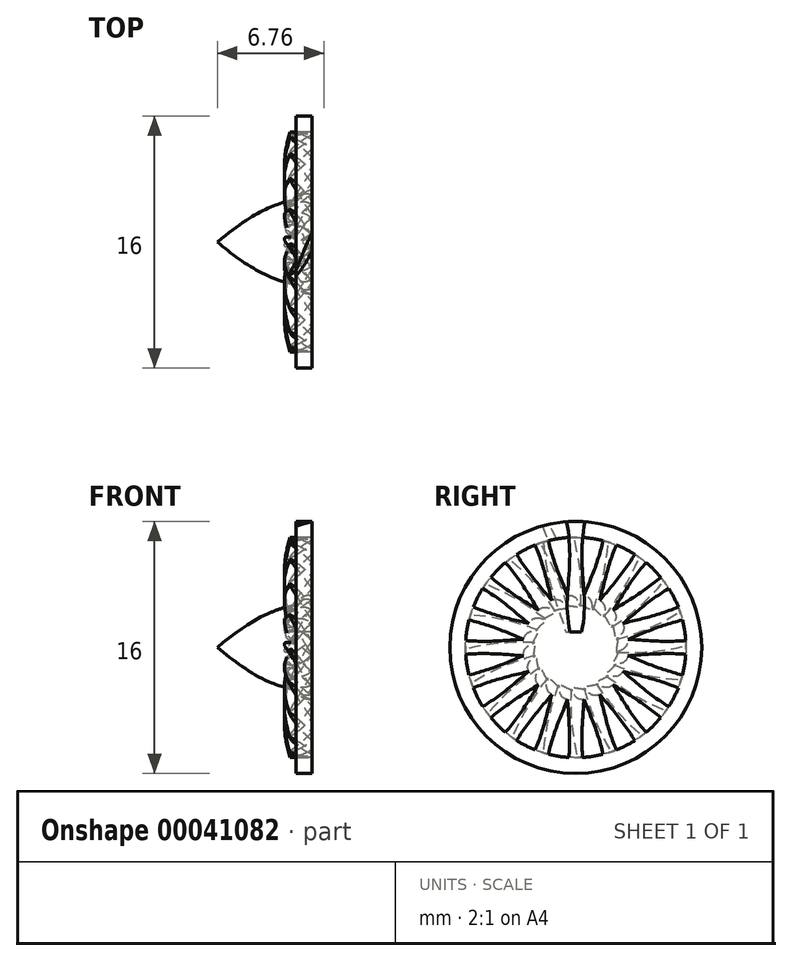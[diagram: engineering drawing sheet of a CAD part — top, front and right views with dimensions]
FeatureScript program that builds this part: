
annotation { "Feature Type Name" : "Feature", "Feature Type Description" : "" }
export const myFeature = defineFeature(function(context is Context, id is Id, definition is map)
    precondition{}
    {
        {
            var Q0;
            Q0=qCreatedBy(makeId("Top.planeOp"),FACE);
            var sketch = newSketch(context, id + "F0", { "sketchPlane" : qUnion([Q0])});
            skLineSegment(sketch, "E0", {"start": v(-70.31, 0) * mm, "end": v(56.67, 0) * mm, "construction": true});
            skLineSegment(sketch, "E1", {"start": v(0, 7) * mm, "end": v(-1, 7) * mm});
            skLineSegment(sketch, "E2", {"start": v(-1, 7) * mm, "end": v(-1, 8) * mm});
            skLineSegment(sketch, "E3", {"start": v(-1, 8) * mm, "end": v(-1, 8) * mm});
            skLineSegment(sketch, "E4", {"start": v(-1, 8) * mm, "end": v(0, 8) * mm});
            skLineSegment(sketch, "E5", {"start": v(0, 8) * mm, "end": v(0, 7) * mm});
            skLineSegment(sketch, "E6", {"start": v(0, 0) * mm, "end": v(0, 3) * mm});
            skLineSegment(sketch, "E7", {"start": v(-6, 0) * mm, "end": v(0, 0) * mm});
            skFitSpline(sketch, "E8", {"points": [v(0, 3) * mm, v(-6, 0) * mm], "startDerivative": vector(-5.94, -1.65) * mm, "endDerivative": vector(-8.8, -7.36) * mm});
            skSolve(sketch);
        }
        {
            var Q0;
            Q0=makeQuery(id+"F0.imprint","IMPRINT",FACE,{"disambiguationData":[TD([[makeQuery(id+"F0.imprint","IMPRINT",EDGE,{"derivedFrom":sQuery(id+"F0.wireOp",EDGE,"E1")}),-1.0]])]});
            var Q1;
            Q1=makeQuery(id+"F0.imprint","IMPRINT",FACE,{"disambiguationData":[TD([[makeQuery(id+"F0.imprint","IMPRINT",EDGE,{"derivedFrom":sQuery(id+"F0.wireOp",EDGE,"E6")}),1.0]])]});
            var Q2;
            Q2=sQuery(id+"F0.wireOp",EDGE,"E0");
            revolve(context, id + "F1", {"entities" : qUnion([Q0, Q1]), "axis" : qUnion([Q2]), "revolveType" : RevolveType.FULL});
        }
        {
            var Q0;
            Q0=qCreatedBy(makeId("Front.planeOp"),FACE);
            cPlane(context, id + "F2", {"entities" : qUnion([Q0]), "cplaneType" : CPlaneType.OFFSET, "offset" : 3.5 * mm, "width" : 150 * mm, "height" : 150 * mm});
        }
        {
            var Q0;
            Q0=qCreatedBy(makeId("Top.planeOp"),FACE);
            cPlane(context, id + "F3", {"entities" : qUnion([Q0]), "cplaneType" : CPlaneType.OFFSET, "offset" : 1 * mm, "width" : 150 * mm, "height" : 150 * mm});
        }
        {
            var Q0;
            Q0=qCreatedBy(makeId("Top.planeOp"),FACE);
            cPlane(context, id + "F4", {"entities" : qUnion([Q0]), "cplaneType" : CPlaneType.OFFSET, "offset" : 4.5 * mm, "width" : 150 * mm, "height" : 150 * mm});
        }
        {
            var Q0;
            Q0=qCreatedBy(makeId("Top.planeOp"),FACE);
            cPlane(context, id + "F5", {"entities" : qUnion([Q0]), "cplaneType" : CPlaneType.OFFSET, "offset" : 8 * mm, "width" : 150 * mm, "height" : 150 * mm});
        }
        {
            var Q0;
            Q0=qCreatedBy(id+"F3.planeOp",FACE);
            var sketch = newSketch(context, id + "F6", { "sketchPlane" : qUnion([Q0])});
            skEllipse(sketch, "E9", {"center": v(0, 0) * mm, "majorRadius": 1.72 * mm, "minorRadius": 0.34 * mm, "majorAxis": v(-0.95, -0.32)});
            skPoint(sketch, "E10.endSnap0", {"position": v(-1.64, -0.55) * mm});
            skSolve(sketch);
        }
        {
            var Q0;
            Q0=qCreatedBy(id+"F4.planeOp",FACE);
            var sketch = newSketch(context, id + "F7", { "sketchPlane" : qUnion([Q0])});
            skEllipse(sketch, "E11", {"center": v(0, 0) * mm, "majorRadius": 2.45 * mm, "minorRadius": 0.31 * mm, "majorAxis": v(-0.7, -0.7)});
            skSolve(sketch);
        }
        {
            var Q0;
            Q0=qCreatedBy(id+"F5.planeOp",FACE);
            var sketch = newSketch(context, id + "F8", { "sketchPlane" : qUnion([Q0])});
            skEllipse(sketch, "E12", {"center": v(0, 0) * mm, "majorRadius": 2.36 * mm, "minorRadius": 0.25 * mm, "majorAxis": v(-0.41, -0.91)});
            skSolve(sketch);
        }
        {
            var Q0;
            Q0=makeQuery(id+"F6.imprint","IMPRINT",FACE,{"disambiguationData":[TD([[makeQuery(id+"F6.imprint","IMPRINT",EDGE,{"derivedFrom":sQuery(id+"F6.wireOp",EDGE,"E9")}),1.0]])]});
            var Q1;
            Q1=makeQuery(id+"F7.imprint","IMPRINT",FACE,{"disambiguationData":[TD([[makeQuery(id+"F7.imprint","IMPRINT",EDGE,{"derivedFrom":sQuery(id+"F7.wireOp",EDGE,"E11")}),1.0]])]});
            var Q2;
            Q2=makeQuery(id+"F8.imprint","IMPRINT",FACE,{"disambiguationData":[TD([[makeQuery(id+"F8.imprint","IMPRINT",EDGE,{"derivedFrom":sQuery(id+"F8.wireOp",EDGE,"E12")}),1.0]])]});
            loft(context, id + "F9", {"sheetProfilesArray" : [{ "sheetProfileEntities" : qUnion([Q0]) }, { "sheetProfileEntities" : qUnion([Q1]) }, { "sheetProfileEntities" : qUnion([Q2]) }]});
        }
        {
            var Q0;
            Q0=makeQuery(id+"F9.opLoft","SWEPT_BODY",BODY,{"disambiguationData":[OSD([makeQuery(id+"F6.imprint","IMPRINT",FACE,{"disambiguationData":[TD([[makeQuery(id+"F6.imprint","IMPRINT",EDGE,{"derivedFrom":sQuery(id+"F6.wireOp",EDGE,"E9")}),1.0]])]}),sQuery(id+"F7.wireOp",EDGE,"E11"),makeQuery(id+"F8.imprint","IMPRINT",FACE,{"disambiguationData":[TD([[makeQuery(id+"F8.imprint","IMPRINT",EDGE,{"derivedFrom":sQuery(id+"F8.wireOp",EDGE,"E12")}),1.0]])]})])]});
            var Q1;
            Q1=qCreatedBy(makeId("Front.planeOp"),FACE);
            mirror(context, id + "F10", {"entities" : qUnion([Q0]), "mirrorPlane" : qUnion([Q1])});
        }
        {
            var Q0;
            Q0=makeQuery(id+"F10.opPattern","COPY",FACE,{"derivedFrom":makeQuery(id+"F9.opLoft","CAP_FACE",FACE,{"disambiguationData":[OSD([makeQuery(id+"F8.imprint","IMPRINT",FACE,{"disambiguationData":[TD([[makeQuery(id+"F8.imprint","IMPRINT",EDGE,{"derivedFrom":sQuery(id+"F8.wireOp",EDGE,"E12")}),1.0]])]})])],"isStart":true}),"instanceName":"1"});
            var sketch = newSketch(context, id + "F11", { "sketchPlane" : qUnion([Q0])});
            skLineSegment(sketch, "E13.bottom", {"start": v(0, -2.61) * mm, "end": v(2.13, -2.61) * mm});
            skLineSegment(sketch, "E13.top", {"start": v(0, 2.6) * mm, "end": v(2.13, 2.6) * mm});
            skLineSegment(sketch, "E13.left", {"start": v(0, -2.61) * mm, "end": v(0, 2.6) * mm});
            skLineSegment(sketch, "E13.right", {"start": v(2.13, -2.61) * mm, "end": v(2.13, 2.6) * mm});
            skSolve(sketch);
        }
        {
            var Q0;
            {var subQ0=makeQuery(id+"F10.opPattern","COPY",EDGE,{"derivedFrom":makeQuery(id+"F9.opLoft","MID_CAP_EDGE",EDGE,{"disambiguationData":[OSD([sQuery(id+"F6.wireOp",EDGE,"E9"),sQuery(id+"F8.wireOp",EDGE,"E12")])],"capPos":2.0}),"instanceName":"1"});var subQ1=sQuery(id+"F11.wireOp",EDGE,"E13.left");var subQ3=makeQuery(id+"F11.imprint","INTERSECT",VERTEX,{"disambiguationData":[OD(0.0)],"derivedFrom":[subQ0,subQ1]});Q0=makeQuery(id+"F11.imprint","IMPRINT",FACE,{"disambiguationData":[TD([[makeQuery(id+"F11.imprint","IMPRINT",EDGE,{"disambiguationData":[TD([[subQ3,-1.0]])],"derivedFrom":subQ1}),-1.0]])]});}
            var Q1;
            {var subQ0=sQuery(id+"F11.wireOp",EDGE,"E13.bottom");Q1=makeQuery(id+"F11.imprint","IMPRINT",FACE,{"disambiguationData":[TD([[makeQuery(id+"F11.imprint","IMPRINT",EDGE,{"derivedFrom":subQ0}),1.0]])]});}
            extrude(context, id + "F12", {"entities" : qUnion([Q0, Q1]), "operationType" : NewBodyOperationType.REMOVE, "oppositeDirection" : true, "depth" : 25 * mm});
        }
        {
            var Q0;
            Q0=makeQuery(id+"F10.opPattern","COPY",BODY,{"derivedFrom":makeQuery(id+"F9.opLoft","SWEPT_BODY",BODY,{"disambiguationData":[OSD([makeQuery(id+"F6.imprint","IMPRINT",FACE,{"disambiguationData":[TD([[makeQuery(id+"F6.imprint","IMPRINT",EDGE,{"derivedFrom":sQuery(id+"F6.wireOp",EDGE,"E9")}),1.0]])]}),sQuery(id+"F7.wireOp",EDGE,"E11"),makeQuery(id+"F8.imprint","IMPRINT",FACE,{"disambiguationData":[TD([[makeQuery(id+"F8.imprint","IMPRINT",EDGE,{"derivedFrom":sQuery(id+"F8.wireOp",EDGE,"E12")}),1.0]])]})])]}),"instanceName":"1"});
            var Q1;
            Q1=makeQuery(id+"F1.opRevolve","SWEPT_FACE",FACE,{"disambiguationData":[OSD([sQuery(id+"F0.wireOp",EDGE,"E1")])]});
            circularPattern(context, id + "F13", {"entities" : qUnion([Q0]), "axis" : qUnion([Q1]), "angle" : 360 * degree, "instanceCount" : 20, "equalSpace" : true});
        }
        {
            var Q0;
            Q0=makeQuery(id+"F1.opRevolve","SWEPT_BODY",BODY,{"disambiguationData":[OSD([sQuery(id+"F0.wireOp",EDGE,"E1"),sQuery(id+"F0.wireOp",EDGE,"E2"),sQuery(id+"F0.wireOp",EDGE,"E4"),sQuery(id+"F0.wireOp",EDGE,"E5")])]});
            var Q1;
            Q1=makeQuery(id+"F1.opRevolve","SWEPT_BODY",BODY,{"disambiguationData":[OSD([sQuery(id+"F0.wireOp",EDGE,"E6"),sQuery(id+"F0.wireOp",EDGE,"E7"),sQuery(id+"F0.wireOp",EDGE,"E8")])]});
            var Q2;
            Q2=makeQuery(id+"F10.opPattern","COPY",BODY,{"derivedFrom":makeQuery(id+"F9.opLoft","SWEPT_BODY",BODY,{"disambiguationData":[OSD([makeQuery(id+"F6.imprint","IMPRINT",FACE,{"disambiguationData":[TD([[makeQuery(id+"F6.imprint","IMPRINT",EDGE,{"derivedFrom":sQuery(id+"F6.wireOp",EDGE,"E9")}),1.0]])]}),sQuery(id+"F7.wireOp",EDGE,"E11"),makeQuery(id+"F8.imprint","IMPRINT",FACE,{"disambiguationData":[TD([[makeQuery(id+"F8.imprint","IMPRINT",EDGE,{"derivedFrom":sQuery(id+"F8.wireOp",EDGE,"E12")}),1.0]])]})])]}),"instanceName":"1"});
            var Q3;
            Q3=makeQuery(id+"F13.opPattern","COPY",BODY,{"derivedFrom":makeQuery(id+"F10.opPattern","COPY",BODY,{"derivedFrom":makeQuery(id+"F9.opLoft","SWEPT_BODY",BODY,{"disambiguationData":[OSD([makeQuery(id+"F6.imprint","IMPRINT",FACE,{"disambiguationData":[TD([[makeQuery(id+"F6.imprint","IMPRINT",EDGE,{"derivedFrom":sQuery(id+"F6.wireOp",EDGE,"E9")}),1.0]])]}),sQuery(id+"F7.wireOp",EDGE,"E11"),makeQuery(id+"F8.imprint","IMPRINT",FACE,{"disambiguationData":[TD([[makeQuery(id+"F8.imprint","IMPRINT",EDGE,{"derivedFrom":sQuery(id+"F8.wireOp",EDGE,"E12")}),1.0]])]})])]}),"instanceName":"1"}),"instanceName":"1"});
            var Q4;
            Q4=makeQuery(id+"F13.opPattern","COPY",BODY,{"derivedFrom":makeQuery(id+"F10.opPattern","COPY",BODY,{"derivedFrom":makeQuery(id+"F9.opLoft","SWEPT_BODY",BODY,{"disambiguationData":[OSD([makeQuery(id+"F6.imprint","IMPRINT",FACE,{"disambiguationData":[TD([[makeQuery(id+"F6.imprint","IMPRINT",EDGE,{"derivedFrom":sQuery(id+"F6.wireOp",EDGE,"E9")}),1.0]])]}),sQuery(id+"F7.wireOp",EDGE,"E11"),makeQuery(id+"F8.imprint","IMPRINT",FACE,{"disambiguationData":[TD([[makeQuery(id+"F8.imprint","IMPRINT",EDGE,{"derivedFrom":sQuery(id+"F8.wireOp",EDGE,"E12")}),1.0]])]})])]}),"instanceName":"1"}),"instanceName":"2"});
            var Q5;
            Q5=makeQuery(id+"F13.opPattern","COPY",BODY,{"derivedFrom":makeQuery(id+"F10.opPattern","COPY",BODY,{"derivedFrom":makeQuery(id+"F9.opLoft","SWEPT_BODY",BODY,{"disambiguationData":[OSD([makeQuery(id+"F6.imprint","IMPRINT",FACE,{"disambiguationData":[TD([[makeQuery(id+"F6.imprint","IMPRINT",EDGE,{"derivedFrom":sQuery(id+"F6.wireOp",EDGE,"E9")}),1.0]])]}),sQuery(id+"F7.wireOp",EDGE,"E11"),makeQuery(id+"F8.imprint","IMPRINT",FACE,{"disambiguationData":[TD([[makeQuery(id+"F8.imprint","IMPRINT",EDGE,{"derivedFrom":sQuery(id+"F8.wireOp",EDGE,"E12")}),1.0]])]})])]}),"instanceName":"1"}),"instanceName":"4"});
            var Q6;
            Q6=makeQuery(id+"F13.opPattern","COPY",BODY,{"derivedFrom":makeQuery(id+"F10.opPattern","COPY",BODY,{"derivedFrom":makeQuery(id+"F9.opLoft","SWEPT_BODY",BODY,{"disambiguationData":[OSD([makeQuery(id+"F6.imprint","IMPRINT",FACE,{"disambiguationData":[TD([[makeQuery(id+"F6.imprint","IMPRINT",EDGE,{"derivedFrom":sQuery(id+"F6.wireOp",EDGE,"E9")}),1.0]])]}),sQuery(id+"F7.wireOp",EDGE,"E11"),makeQuery(id+"F8.imprint","IMPRINT",FACE,{"disambiguationData":[TD([[makeQuery(id+"F8.imprint","IMPRINT",EDGE,{"derivedFrom":sQuery(id+"F8.wireOp",EDGE,"E12")}),1.0]])]})])]}),"instanceName":"1"}),"instanceName":"5"});
            var Q7;
            Q7=makeQuery(id+"F13.opPattern","COPY",BODY,{"derivedFrom":makeQuery(id+"F10.opPattern","COPY",BODY,{"derivedFrom":makeQuery(id+"F9.opLoft","SWEPT_BODY",BODY,{"disambiguationData":[OSD([makeQuery(id+"F6.imprint","IMPRINT",FACE,{"disambiguationData":[TD([[makeQuery(id+"F6.imprint","IMPRINT",EDGE,{"derivedFrom":sQuery(id+"F6.wireOp",EDGE,"E9")}),1.0]])]}),sQuery(id+"F7.wireOp",EDGE,"E11"),makeQuery(id+"F8.imprint","IMPRINT",FACE,{"disambiguationData":[TD([[makeQuery(id+"F8.imprint","IMPRINT",EDGE,{"derivedFrom":sQuery(id+"F8.wireOp",EDGE,"E12")}),1.0]])]})])]}),"instanceName":"1"}),"instanceName":"6"});
            var Q8;
            Q8=makeQuery(id+"F13.opPattern","COPY",BODY,{"derivedFrom":makeQuery(id+"F10.opPattern","COPY",BODY,{"derivedFrom":makeQuery(id+"F9.opLoft","SWEPT_BODY",BODY,{"disambiguationData":[OSD([makeQuery(id+"F6.imprint","IMPRINT",FACE,{"disambiguationData":[TD([[makeQuery(id+"F6.imprint","IMPRINT",EDGE,{"derivedFrom":sQuery(id+"F6.wireOp",EDGE,"E9")}),1.0]])]}),sQuery(id+"F7.wireOp",EDGE,"E11"),makeQuery(id+"F8.imprint","IMPRINT",FACE,{"disambiguationData":[TD([[makeQuery(id+"F8.imprint","IMPRINT",EDGE,{"derivedFrom":sQuery(id+"F8.wireOp",EDGE,"E12")}),1.0]])]})])]}),"instanceName":"1"}),"instanceName":"7"});
            var Q9;
            Q9=makeQuery(id+"F13.opPattern","COPY",BODY,{"derivedFrom":makeQuery(id+"F10.opPattern","COPY",BODY,{"derivedFrom":makeQuery(id+"F9.opLoft","SWEPT_BODY",BODY,{"disambiguationData":[OSD([makeQuery(id+"F6.imprint","IMPRINT",FACE,{"disambiguationData":[TD([[makeQuery(id+"F6.imprint","IMPRINT",EDGE,{"derivedFrom":sQuery(id+"F6.wireOp",EDGE,"E9")}),1.0]])]}),sQuery(id+"F7.wireOp",EDGE,"E11"),makeQuery(id+"F8.imprint","IMPRINT",FACE,{"disambiguationData":[TD([[makeQuery(id+"F8.imprint","IMPRINT",EDGE,{"derivedFrom":sQuery(id+"F8.wireOp",EDGE,"E12")}),1.0]])]})])]}),"instanceName":"1"}),"instanceName":"8"});
            var Q10;
            Q10=makeQuery(id+"F13.opPattern","COPY",BODY,{"derivedFrom":makeQuery(id+"F10.opPattern","COPY",BODY,{"derivedFrom":makeQuery(id+"F9.opLoft","SWEPT_BODY",BODY,{"disambiguationData":[OSD([makeQuery(id+"F6.imprint","IMPRINT",FACE,{"disambiguationData":[TD([[makeQuery(id+"F6.imprint","IMPRINT",EDGE,{"derivedFrom":sQuery(id+"F6.wireOp",EDGE,"E9")}),1.0]])]}),sQuery(id+"F7.wireOp",EDGE,"E11"),makeQuery(id+"F8.imprint","IMPRINT",FACE,{"disambiguationData":[TD([[makeQuery(id+"F8.imprint","IMPRINT",EDGE,{"derivedFrom":sQuery(id+"F8.wireOp",EDGE,"E12")}),1.0]])]})])]}),"instanceName":"1"}),"instanceName":"9"});
            var Q11;
            Q11=makeQuery(id+"F13.opPattern","COPY",BODY,{"derivedFrom":makeQuery(id+"F10.opPattern","COPY",BODY,{"derivedFrom":makeQuery(id+"F9.opLoft","SWEPT_BODY",BODY,{"disambiguationData":[OSD([makeQuery(id+"F6.imprint","IMPRINT",FACE,{"disambiguationData":[TD([[makeQuery(id+"F6.imprint","IMPRINT",EDGE,{"derivedFrom":sQuery(id+"F6.wireOp",EDGE,"E9")}),1.0]])]}),sQuery(id+"F7.wireOp",EDGE,"E11"),makeQuery(id+"F8.imprint","IMPRINT",FACE,{"disambiguationData":[TD([[makeQuery(id+"F8.imprint","IMPRINT",EDGE,{"derivedFrom":sQuery(id+"F8.wireOp",EDGE,"E12")}),1.0]])]})])]}),"instanceName":"1"}),"instanceName":"10"});
            var Q12;
            Q12=makeQuery(id+"F13.opPattern","COPY",BODY,{"derivedFrom":makeQuery(id+"F10.opPattern","COPY",BODY,{"derivedFrom":makeQuery(id+"F9.opLoft","SWEPT_BODY",BODY,{"disambiguationData":[OSD([makeQuery(id+"F6.imprint","IMPRINT",FACE,{"disambiguationData":[TD([[makeQuery(id+"F6.imprint","IMPRINT",EDGE,{"derivedFrom":sQuery(id+"F6.wireOp",EDGE,"E9")}),1.0]])]}),sQuery(id+"F7.wireOp",EDGE,"E11"),makeQuery(id+"F8.imprint","IMPRINT",FACE,{"disambiguationData":[TD([[makeQuery(id+"F8.imprint","IMPRINT",EDGE,{"derivedFrom":sQuery(id+"F8.wireOp",EDGE,"E12")}),1.0]])]})])]}),"instanceName":"1"}),"instanceName":"11"});
            var Q13;
            Q13=makeQuery(id+"F13.opPattern","COPY",BODY,{"derivedFrom":makeQuery(id+"F10.opPattern","COPY",BODY,{"derivedFrom":makeQuery(id+"F9.opLoft","SWEPT_BODY",BODY,{"disambiguationData":[OSD([makeQuery(id+"F6.imprint","IMPRINT",FACE,{"disambiguationData":[TD([[makeQuery(id+"F6.imprint","IMPRINT",EDGE,{"derivedFrom":sQuery(id+"F6.wireOp",EDGE,"E9")}),1.0]])]}),sQuery(id+"F7.wireOp",EDGE,"E11"),makeQuery(id+"F8.imprint","IMPRINT",FACE,{"disambiguationData":[TD([[makeQuery(id+"F8.imprint","IMPRINT",EDGE,{"derivedFrom":sQuery(id+"F8.wireOp",EDGE,"E12")}),1.0]])]})])]}),"instanceName":"1"}),"instanceName":"12"});
            var Q14;
            Q14=makeQuery(id+"F13.opPattern","COPY",BODY,{"derivedFrom":makeQuery(id+"F10.opPattern","COPY",BODY,{"derivedFrom":makeQuery(id+"F9.opLoft","SWEPT_BODY",BODY,{"disambiguationData":[OSD([makeQuery(id+"F6.imprint","IMPRINT",FACE,{"disambiguationData":[TD([[makeQuery(id+"F6.imprint","IMPRINT",EDGE,{"derivedFrom":sQuery(id+"F6.wireOp",EDGE,"E9")}),1.0]])]}),sQuery(id+"F7.wireOp",EDGE,"E11"),makeQuery(id+"F8.imprint","IMPRINT",FACE,{"disambiguationData":[TD([[makeQuery(id+"F8.imprint","IMPRINT",EDGE,{"derivedFrom":sQuery(id+"F8.wireOp",EDGE,"E12")}),1.0]])]})])]}),"instanceName":"1"}),"instanceName":"13"});
            var Q15;
            Q15=makeQuery(id+"F13.opPattern","COPY",BODY,{"derivedFrom":makeQuery(id+"F10.opPattern","COPY",BODY,{"derivedFrom":makeQuery(id+"F9.opLoft","SWEPT_BODY",BODY,{"disambiguationData":[OSD([makeQuery(id+"F6.imprint","IMPRINT",FACE,{"disambiguationData":[TD([[makeQuery(id+"F6.imprint","IMPRINT",EDGE,{"derivedFrom":sQuery(id+"F6.wireOp",EDGE,"E9")}),1.0]])]}),sQuery(id+"F7.wireOp",EDGE,"E11"),makeQuery(id+"F8.imprint","IMPRINT",FACE,{"disambiguationData":[TD([[makeQuery(id+"F8.imprint","IMPRINT",EDGE,{"derivedFrom":sQuery(id+"F8.wireOp",EDGE,"E12")}),1.0]])]})])]}),"instanceName":"1"}),"instanceName":"14"});
            var Q16;
            Q16=makeQuery(id+"F13.opPattern","COPY",BODY,{"derivedFrom":makeQuery(id+"F10.opPattern","COPY",BODY,{"derivedFrom":makeQuery(id+"F9.opLoft","SWEPT_BODY",BODY,{"disambiguationData":[OSD([makeQuery(id+"F6.imprint","IMPRINT",FACE,{"disambiguationData":[TD([[makeQuery(id+"F6.imprint","IMPRINT",EDGE,{"derivedFrom":sQuery(id+"F6.wireOp",EDGE,"E9")}),1.0]])]}),sQuery(id+"F7.wireOp",EDGE,"E11"),makeQuery(id+"F8.imprint","IMPRINT",FACE,{"disambiguationData":[TD([[makeQuery(id+"F8.imprint","IMPRINT",EDGE,{"derivedFrom":sQuery(id+"F8.wireOp",EDGE,"E12")}),1.0]])]})])]}),"instanceName":"1"}),"instanceName":"16"});
            var Q17;
            Q17=makeQuery(id+"F13.opPattern","COPY",BODY,{"derivedFrom":makeQuery(id+"F10.opPattern","COPY",BODY,{"derivedFrom":makeQuery(id+"F9.opLoft","SWEPT_BODY",BODY,{"disambiguationData":[OSD([makeQuery(id+"F6.imprint","IMPRINT",FACE,{"disambiguationData":[TD([[makeQuery(id+"F6.imprint","IMPRINT",EDGE,{"derivedFrom":sQuery(id+"F6.wireOp",EDGE,"E9")}),1.0]])]}),sQuery(id+"F7.wireOp",EDGE,"E11"),makeQuery(id+"F8.imprint","IMPRINT",FACE,{"disambiguationData":[TD([[makeQuery(id+"F8.imprint","IMPRINT",EDGE,{"derivedFrom":sQuery(id+"F8.wireOp",EDGE,"E12")}),1.0]])]})])]}),"instanceName":"1"}),"instanceName":"17"});
            var Q18;
            Q18=makeQuery(id+"F13.opPattern","COPY",BODY,{"derivedFrom":makeQuery(id+"F10.opPattern","COPY",BODY,{"derivedFrom":makeQuery(id+"F9.opLoft","SWEPT_BODY",BODY,{"disambiguationData":[OSD([makeQuery(id+"F6.imprint","IMPRINT",FACE,{"disambiguationData":[TD([[makeQuery(id+"F6.imprint","IMPRINT",EDGE,{"derivedFrom":sQuery(id+"F6.wireOp",EDGE,"E9")}),1.0]])]}),sQuery(id+"F7.wireOp",EDGE,"E11"),makeQuery(id+"F8.imprint","IMPRINT",FACE,{"disambiguationData":[TD([[makeQuery(id+"F8.imprint","IMPRINT",EDGE,{"derivedFrom":sQuery(id+"F8.wireOp",EDGE,"E12")}),1.0]])]})])]}),"instanceName":"1"}),"instanceName":"18"});
            var Q19;
            Q19=makeQuery(id+"F13.opPattern","COPY",BODY,{"derivedFrom":makeQuery(id+"F10.opPattern","COPY",BODY,{"derivedFrom":makeQuery(id+"F9.opLoft","SWEPT_BODY",BODY,{"disambiguationData":[OSD([makeQuery(id+"F6.imprint","IMPRINT",FACE,{"disambiguationData":[TD([[makeQuery(id+"F6.imprint","IMPRINT",EDGE,{"derivedFrom":sQuery(id+"F6.wireOp",EDGE,"E9")}),1.0]])]}),sQuery(id+"F7.wireOp",EDGE,"E11"),makeQuery(id+"F8.imprint","IMPRINT",FACE,{"disambiguationData":[TD([[makeQuery(id+"F8.imprint","IMPRINT",EDGE,{"derivedFrom":sQuery(id+"F8.wireOp",EDGE,"E12")}),1.0]])]})])]}),"instanceName":"1"}),"instanceName":"19"});
            var Q20;
            Q20=makeQuery(id+"F13.opPattern","COPY",BODY,{"derivedFrom":makeQuery(id+"F10.opPattern","COPY",BODY,{"derivedFrom":makeQuery(id+"F9.opLoft","SWEPT_BODY",BODY,{"disambiguationData":[OSD([makeQuery(id+"F6.imprint","IMPRINT",FACE,{"disambiguationData":[TD([[makeQuery(id+"F6.imprint","IMPRINT",EDGE,{"derivedFrom":sQuery(id+"F6.wireOp",EDGE,"E9")}),1.0]])]}),sQuery(id+"F7.wireOp",EDGE,"E11"),makeQuery(id+"F8.imprint","IMPRINT",FACE,{"disambiguationData":[TD([[makeQuery(id+"F8.imprint","IMPRINT",EDGE,{"derivedFrom":sQuery(id+"F8.wireOp",EDGE,"E12")}),1.0]])]})])]}),"instanceName":"1"}),"instanceName":"15"});
            var Q21;
            Q21=makeQuery(id+"F13.opPattern","COPY",BODY,{"derivedFrom":makeQuery(id+"F10.opPattern","COPY",BODY,{"derivedFrom":makeQuery(id+"F9.opLoft","SWEPT_BODY",BODY,{"disambiguationData":[OSD([makeQuery(id+"F6.imprint","IMPRINT",FACE,{"disambiguationData":[TD([[makeQuery(id+"F6.imprint","IMPRINT",EDGE,{"derivedFrom":sQuery(id+"F6.wireOp",EDGE,"E9")}),1.0]])]}),sQuery(id+"F7.wireOp",EDGE,"E11"),makeQuery(id+"F8.imprint","IMPRINT",FACE,{"disambiguationData":[TD([[makeQuery(id+"F8.imprint","IMPRINT",EDGE,{"derivedFrom":sQuery(id+"F8.wireOp",EDGE,"E12")}),1.0]])]})])]}),"instanceName":"1"}),"instanceName":"3"});
            booleanBodies(context, id + "F14", {"operationType" : BooleanOperationType.UNION, "tools" : qUnion([Q0, Q1, Q2, Q3, Q4, Q5, Q6, Q7, Q8, Q9, Q10, Q11, Q12, Q13, Q14, Q15, Q16, Q17, Q18, Q19, Q20, Q21])});
        }
        {
            var Q0;
            Q0=qCreatedBy(makeId("Front.planeOp"),FACE);
            var sketch = newSketch(context, id + "F15", { "sketchPlane" : qUnion([Q0])});
            skLineSegment(sketch, "E14", {"start": v(-3, 7) * mm, "end": v(-1, 7) * mm});
            skLineSegment(sketch, "E15", {"start": v(-1, 7) * mm, "end": v(-1, 8) * mm});
            skLineSegment(sketch, "E16", {"start": v(-1, 8) * mm, "end": v(0, 8) * mm});
            skLineSegment(sketch, "E17", {"start": v(0, 8) * mm, "end": v(0, 10) * mm});
            skLineSegment(sketch, "E18", {"start": v(0, 10) * mm, "end": v(-3, 10) * mm});
            skLineSegment(sketch, "E19", {"start": v(-3, 10) * mm, "end": v(-3, 7) * mm});
            skSolve(sketch);
        }
        {
            var Q0;
            Q0 = qSketchRegion(id + "F15", true);
            var Q1;
            Q1=makeQuery(id+"F14.opBoolean","SPLIT",FACE,{"disambiguationData":[TD([makeQuery(id+"F13.opPattern","COPY",FACE,{"derivedFrom":makeQuery(id+"F10.opPattern","COPY",FACE,{"derivedFrom":makeQuery(id+"F9.opLoft","CAP_FACE",FACE,{"disambiguationData":[OSD([makeQuery(id+"F8.imprint","IMPRINT",FACE,{"disambiguationData":[TD([[makeQuery(id+"F8.imprint","IMPRINT",EDGE,{"derivedFrom":sQuery(id+"F8.wireOp",EDGE,"E12")}),1.0]])]})])],"isStart":true}),"instanceName":"1"}),"instanceName":"3"})])],"derivedFrom":makeQuery(id+"F1.opRevolve","SWEPT_FACE",FACE,{"disambiguationData":[OSD([sQuery(id+"F0.wireOp",EDGE,"E4")])]})});
            revolve(context, id + "F16", {"operationType" : NewBodyOperationType.REMOVE, "entities" : qUnion([Q0]), "axis" : qUnion([Q1]), "revolveType" : RevolveType.FULL, "oppositeDirection" : true});
        }
    });
